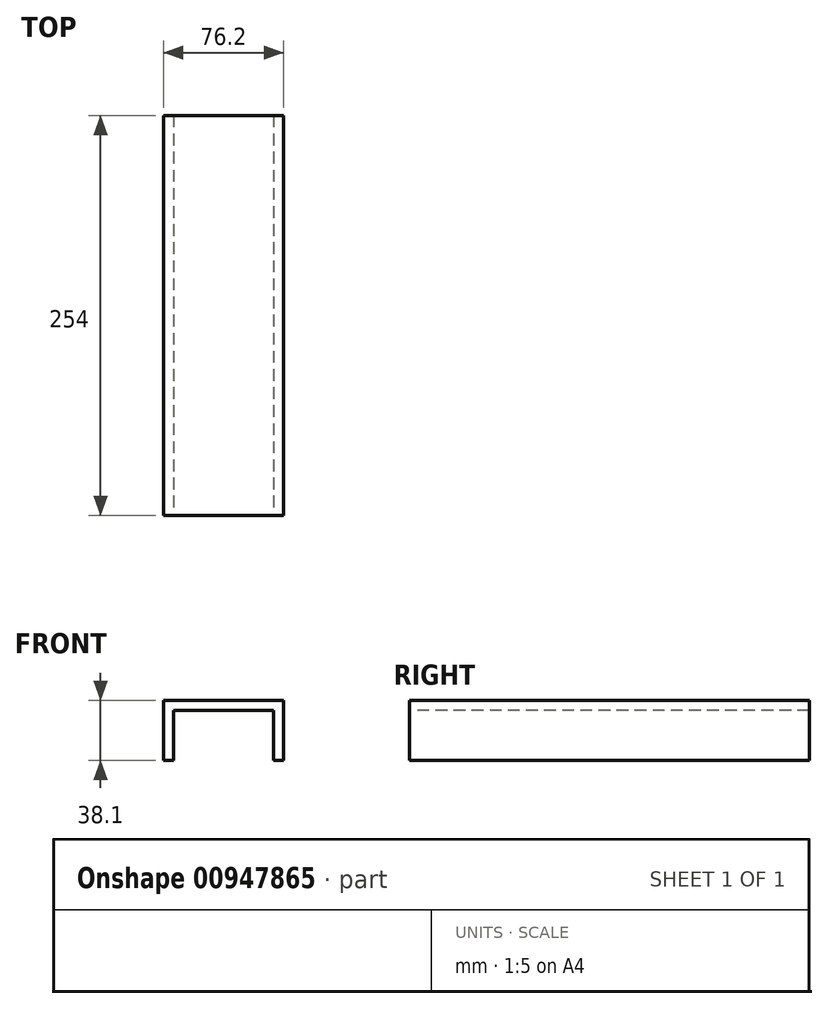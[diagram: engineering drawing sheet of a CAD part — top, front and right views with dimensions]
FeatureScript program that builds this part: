
annotation { "Feature Type Name" : "Feature", "Feature Type Description" : "" }
export const myFeature = defineFeature(function(context is Context, id is Id, definition is map)
    precondition{}
    {
        {
            var Q0;
            Q0=qCreatedBy(makeId("Front.planeOp"),FACE);
            var sketch = newSketch(context, id + "F0", { "sketchPlane" : qUnion([Q0])});
            skLineSegment(sketch, "E0.bottom", {"start": v(-32.87, 0) * mm, "end": v(-26.52, 0) * mm});
            skLineSegment(sketch, "E0.top", {"start": v(-32.87, 38.1) * mm, "end": v(43.33, 38.1) * mm});
            skLineSegment(sketch, "E0.left", {"start": v(-32.87, 0) * mm, "end": v(-32.87, 38.1) * mm});
            skLineSegment(sketch, "E0.right", {"start": v(43.33, 0) * mm, "end": v(43.33, 38.1) * mm});
            skLineSegment(sketch, "E1.top", {"start": v(36.98, 31.75) * mm, "end": v(-26.52, 31.75) * mm});
            skLineSegment(sketch, "E1.left", {"start": v(36.98, 0) * mm, "end": v(36.98, 31.75) * mm});
            skLineSegment(sketch, "E1.right", {"start": v(-26.52, 0) * mm, "end": v(-26.52, 31.75) * mm});
            skLineSegment(sketch, "E2.trimOffspring", {"start": v(36.98, 0) * mm, "end": v(43.33, 0) * mm});
            skSolve(sketch);
        }
        {
            var Q0;
            Q0 = qSketchRegion(id + "F0", true);
            extrude(context, id + "F1", {"entities" : qUnion([Q0]), "oppositeDirection" : true, "depth" : 254 * mm, "offsetDistance" : 25.4 * mm});
        }
    });
